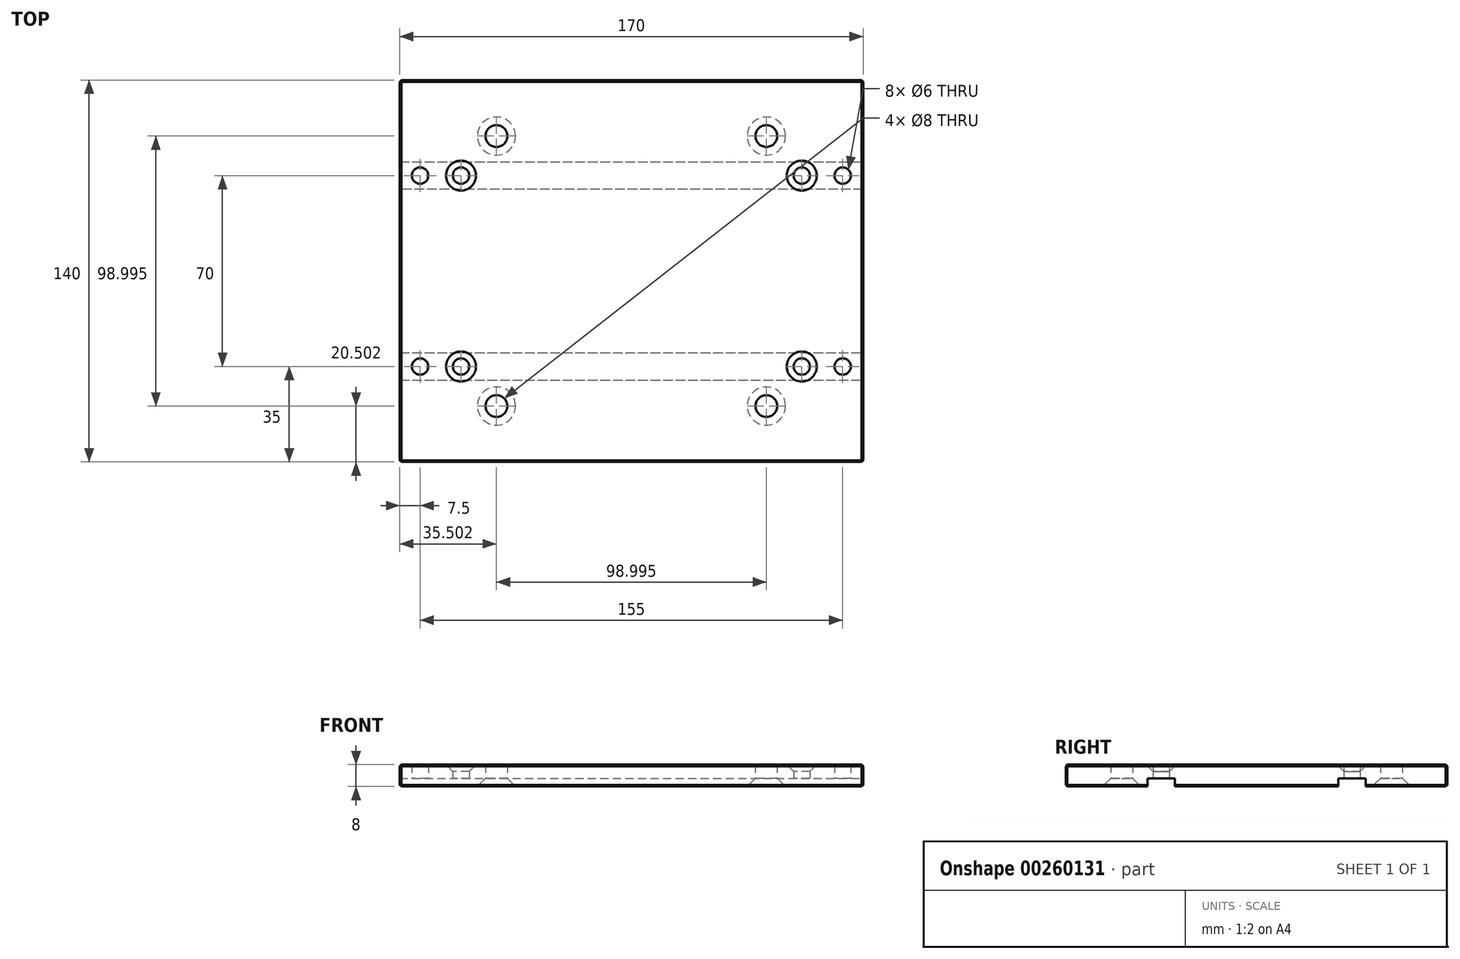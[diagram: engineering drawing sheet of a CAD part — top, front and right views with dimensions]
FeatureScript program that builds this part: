
annotation { "Feature Type Name" : "Feature", "Feature Type Description" : "" }
export const myFeature = defineFeature(function(context is Context, id is Id, definition is map)
    precondition{}
    {
        {
            var Q0;
            Q0=qCreatedBy(makeId("Top.planeOp"),FACE);
            var sketch = newSketch(context, id + "F0", { "sketchPlane" : qUnion([Q0])});
            skLineSegment(sketch, "E0.bottom", {"start": v(-85, -70) * mm, "end": v(85, -70) * mm});
            skLineSegment(sketch, "E0.top", {"start": v(-85, 70) * mm, "end": v(85, 70) * mm});
            skLineSegment(sketch, "E0.left", {"start": v(-85, -70) * mm, "end": v(-85, 70) * mm});
            skLineSegment(sketch, "E0.right", {"start": v(85, -70) * mm, "end": v(85, 70) * mm});
            skPoint(sketch, "E0.middle", {"position": v(0, 0) * mm});
            skCircle(sketch, "E1", {"center": v(0, 0) * mm, "radius": 70 * mm, "construction": true});
            skLineSegment(sketch, "E2", {"start": v(0, 0) * mm, "end": v(-49.5, 49.5) * mm, "construction": true});
            skLineSegment(sketch, "E3", {"start": v(-49.5, 49.5) * mm, "end": v(49.5, 49.5) * mm, "construction": true});
            skCircle(sketch, "E4", {"center": v(-49.5, 49.5) * mm, "radius": 4 * mm});
            skCircle(sketch, "E5", {"center": v(49.5, 49.5) * mm, "radius": 4 * mm});
            skCircle(sketch, "E6.MirrorC", {"center": v(49.5, -49.5) * mm, "radius": 4 * mm});
            skCircle(sketch, "E7.MirrorC", {"center": v(-49.5, -49.5) * mm, "radius": 4 * mm});
            skSolve(sketch);
        }
        {
            var Q0;
            Q0=makeQuery(id+"F0.imprint","IMPRINT",FACE,{"disambiguationData":[TD([[makeQuery(id+"F0.imprint","IMPRINT",EDGE,{"derivedFrom":sQuery(id+"F0.wireOp",EDGE,"E0.bottom")}),1.0]])]});
            extrude(context, id + "F1", {"entities" : qUnion([Q0]), "depth" : 8 * mm});
        }
        {
            var Q0;
            Q0=makeQuery(id+"F1.opExtrude","CAP_EDGE",EDGE,{"disambiguationData":[OSD([sQuery(id+"F0.wireOp",EDGE,"E7.MirrorC")])],"isStart":true});
            var Q1;
            Q1=makeQuery(id+"F1.opExtrude","CAP_EDGE",EDGE,{"disambiguationData":[OSD([sQuery(id+"F0.wireOp",EDGE,"E4")])],"isStart":true});
            var Q2;
            Q2=makeQuery(id+"F1.opExtrude","CAP_EDGE",EDGE,{"disambiguationData":[OSD([sQuery(id+"F0.wireOp",EDGE,"E5")])],"isStart":true});
            var Q3;
            Q3=makeQuery(id+"F1.opExtrude","CAP_EDGE",EDGE,{"disambiguationData":[OSD([sQuery(id+"F0.wireOp",EDGE,"E6.MirrorC")])],"isStart":true});
            chamfer(context, id + "F2", {"entities" : qUnion([Q0, Q1, Q2, Q3]), "width" : 3 * mm, "tangentPropagation" : true});
        }
        {
            var Q0;
            Q0=qCreatedBy(makeId("Top.planeOp"),FACE);
            var sketch = newSketch(context, id + "F3", { "sketchPlane" : qUnion([Q0])});
            skLineSegment(sketch, "E8", {"start": v(0, 0) * mm, "end": v(-90, 0) * mm, "construction": true});
            skLineSegment(sketch, "E9", {"start": v(-90, 0) * mm, "end": v(-90, -30) * mm, "construction": true});
            skLineSegment(sketch, "E10", {"start": v(-90, -30) * mm, "end": v(90, -30) * mm});
            skLineSegment(sketch, "E11", {"start": v(90, -30) * mm, "end": v(90, 30) * mm, "construction": true});
            skLineSegment(sketch, "E12", {"start": v(90, 30) * mm, "end": v(-90, 30) * mm});
            skLineSegment(sketch, "E13", {"start": v(-90, -30) * mm, "end": v(-90, -40) * mm});
            skLineSegment(sketch, "E14", {"start": v(-90, -40) * mm, "end": v(90, -40) * mm});
            skLineSegment(sketch, "E15", {"start": v(90, -40) * mm, "end": v(90, -30) * mm});
            skLineSegment(sketch, "E16", {"start": v(-90, 30) * mm, "end": v(-90, 40) * mm});
            skLineSegment(sketch, "E17", {"start": v(-90, 40) * mm, "end": v(90, 40) * mm});
            skLineSegment(sketch, "E18", {"start": v(90, 40) * mm, "end": v(90, 30) * mm});
            skSolve(sketch);
        }
        {
            var Q0;
            Q0=makeQuery(id+"F3.imprint","IMPRINT",FACE,{"disambiguationData":[TD([[makeQuery(id+"F3.imprint","IMPRINT",EDGE,{"derivedFrom":sQuery(id+"F3.wireOp",EDGE,"E10")}),-1.0]])]});
            var Q1;
            Q1=makeQuery(id+"F3.imprint","IMPRINT",FACE,{"disambiguationData":[TD([[makeQuery(id+"F3.imprint","IMPRINT",EDGE,{"derivedFrom":sQuery(id+"F3.wireOp",EDGE,"E12")}),-1.0]])]});
            extrude(context, id + "F4", {"entities" : qUnion([Q0, Q1]), "operationType" : NewBodyOperationType.REMOVE, "oppositeDirection" : true, "depth" : 25 * mm, "hasSecondDirection" : true, "secondDirectionOppositeDirection" : false, "secondDirectionDepth" : 3 * mm});
        }
        {
            var Q0;
            Q0=qCreatedBy(makeId("Top.planeOp"),FACE);
            var sketch = newSketch(context, id + "F5", { "sketchPlane" : qUnion([Q0])});
            skLineSegment(sketch, "E19", {"start": v(0, 0) * mm, "end": v(-85, 0) * mm, "construction": true});
            skLineSegment(sketch, "E20", {"start": v(-85, 0) * mm, "end": v(-85, -35) * mm, "construction": true});
            skLineSegment(sketch, "E21", {"start": v(-85, -35) * mm, "end": v(-62.5, -35) * mm, "construction": true});
            skLineSegment(sketch, "E22", {"start": v(-62.5, -35) * mm, "end": v(-62.5, -45) * mm, "construction": true});
            skLineSegment(sketch, "E23", {"start": v(-62.5, -45) * mm, "end": v(-77.5, -45) * mm, "construction": true});
            skLineSegment(sketch, "E24", {"start": v(-77.5, -45) * mm, "end": v(-77.5, -35) * mm, "construction": true});
            skCircle(sketch, "E25", {"center": v(-62.5, -35) * mm, "radius": 3 * mm});
            skCircle(sketch, "E26", {"center": v(-77.5, -35) * mm, "radius": 3 * mm});
            skCircle(sketch, "E27.MirrorC", {"center": v(-62.5, 35) * mm, "radius": 3 * mm});
            skCircle(sketch, "E28.MirrorC", {"center": v(-77.5, 35) * mm, "radius": 3 * mm});
            skCircle(sketch, "E29.MirrorC", {"center": v(62.5, 35) * mm, "radius": 3 * mm});
            skCircle(sketch, "E30.MirrorC", {"center": v(77.5, 35) * mm, "radius": 3 * mm});
            skCircle(sketch, "E31.MirrorC", {"center": v(62.5, -35) * mm, "radius": 3 * mm});
            skCircle(sketch, "E32.MirrorC", {"center": v(77.5, -35) * mm, "radius": 3 * mm});
            skSolve(sketch);
        }
        {
            var Q0;
            Q0 = qSketchRegion(id + "F5", true);
            extrude(context, id + "F6", {"entities" : qUnion([Q0]), "operationType" : NewBodyOperationType.REMOVE, "depth" : 25 * mm});
        }
        {
            var Q0;
            Q0=makeQuery(id+"F6.boolean.opBoolean","INTERSECT",EDGE,{"derivedFrom":[makeQuery(id+"F1.opExtrude","CAP_FACE",FACE,{"disambiguationData":[OSD([sQuery(id+"F0.wireOp",EDGE,"E0.bottom"),sQuery(id+"F0.wireOp",EDGE,"E0.top"),sQuery(id+"F0.wireOp",EDGE,"E0.left"),sQuery(id+"F0.wireOp",EDGE,"E0.right"),sQuery(id+"F0.wireOp",EDGE,"E4"),sQuery(id+"F0.wireOp",EDGE,"E5"),sQuery(id+"F0.wireOp",EDGE,"E6.MirrorC"),sQuery(id+"F0.wireOp",EDGE,"E7.MirrorC")])],"isStart":false}),makeQuery(id+"F6.opExtrude","SWEPT_FACE",FACE,{"disambiguationData":[OSD([sQuery(id+"F5.wireOp",EDGE,"E27.MirrorC")])]})]});
            var Q1;
            Q1=makeQuery(id+"F6.boolean.opBoolean","INTERSECT",EDGE,{"derivedFrom":[makeQuery(id+"F1.opExtrude","CAP_FACE",FACE,{"disambiguationData":[OSD([sQuery(id+"F0.wireOp",EDGE,"E0.bottom"),sQuery(id+"F0.wireOp",EDGE,"E0.top"),sQuery(id+"F0.wireOp",EDGE,"E0.left"),sQuery(id+"F0.wireOp",EDGE,"E0.right"),sQuery(id+"F0.wireOp",EDGE,"E4"),sQuery(id+"F0.wireOp",EDGE,"E5"),sQuery(id+"F0.wireOp",EDGE,"E6.MirrorC"),sQuery(id+"F0.wireOp",EDGE,"E7.MirrorC")])],"isStart":false}),makeQuery(id+"F6.opExtrude","SWEPT_FACE",FACE,{"disambiguationData":[OSD([sQuery(id+"F5.wireOp",EDGE,"E25")])]})]});
            var Q2;
            Q2=makeQuery(id+"F6.boolean.opBoolean","INTERSECT",EDGE,{"derivedFrom":[makeQuery(id+"F1.opExtrude","CAP_FACE",FACE,{"disambiguationData":[OSD([sQuery(id+"F0.wireOp",EDGE,"E0.bottom"),sQuery(id+"F0.wireOp",EDGE,"E0.top"),sQuery(id+"F0.wireOp",EDGE,"E0.left"),sQuery(id+"F0.wireOp",EDGE,"E0.right"),sQuery(id+"F0.wireOp",EDGE,"E4"),sQuery(id+"F0.wireOp",EDGE,"E5"),sQuery(id+"F0.wireOp",EDGE,"E6.MirrorC"),sQuery(id+"F0.wireOp",EDGE,"E7.MirrorC")])],"isStart":false}),makeQuery(id+"F6.opExtrude","SWEPT_FACE",FACE,{"disambiguationData":[OSD([sQuery(id+"F5.wireOp",EDGE,"E31.MirrorC")])]})]});
            var Q3;
            Q3=makeQuery(id+"F6.boolean.opBoolean","INTERSECT",EDGE,{"derivedFrom":[makeQuery(id+"F1.opExtrude","CAP_FACE",FACE,{"disambiguationData":[OSD([sQuery(id+"F0.wireOp",EDGE,"E0.bottom"),sQuery(id+"F0.wireOp",EDGE,"E0.top"),sQuery(id+"F0.wireOp",EDGE,"E0.left"),sQuery(id+"F0.wireOp",EDGE,"E0.right"),sQuery(id+"F0.wireOp",EDGE,"E4"),sQuery(id+"F0.wireOp",EDGE,"E5"),sQuery(id+"F0.wireOp",EDGE,"E6.MirrorC"),sQuery(id+"F0.wireOp",EDGE,"E7.MirrorC")])],"isStart":false}),makeQuery(id+"F6.opExtrude","SWEPT_FACE",FACE,{"disambiguationData":[OSD([sQuery(id+"F5.wireOp",EDGE,"E29.MirrorC")])]})]});
            chamfer(context, id + "F7", {"entities" : qUnion([Q0, Q1, Q2, Q3]), "width" : 2.5 * mm, "tangentPropagation" : true});
        }
        {
            var Q0;
            Q0=makeQuery(id+"F1.opExtrude","CAP_EDGE",EDGE,{"disambiguationData":[OSD([sQuery(id+"F0.wireOp",EDGE,"E0.left")])],"isStart":false});
            var Q1;
            Q1=makeQuery(id+"F1.opExtrude","CAP_EDGE",EDGE,{"disambiguationData":[OSD([sQuery(id+"F0.wireOp",EDGE,"E0.top")])],"isStart":false});
            var Q2;
            Q2=makeQuery(id+"F1.opExtrude","CAP_EDGE",EDGE,{"disambiguationData":[OSD([sQuery(id+"F0.wireOp",EDGE,"E0.bottom")])],"isStart":false});
            var Q3;
            Q3=makeQuery(id+"F1.opExtrude","CAP_EDGE",EDGE,{"disambiguationData":[OSD([sQuery(id+"F0.wireOp",EDGE,"E0.right")])],"isStart":false});
            var Q4;
            Q4=makeQuery(id+"F1.opExtrude","SWEPT_EDGE",EDGE,{"disambiguationData":[OSD([sQuery(id+"F0.wireOp",EDGE,"E0.bottom"),sQuery(id+"F0.wireOp",EDGE,"E0.right")])]});
            var Q5;
            Q5=makeQuery(id+"F1.opExtrude","SWEPT_EDGE",EDGE,{"disambiguationData":[OSD([sQuery(id+"F0.wireOp",EDGE,"E0.bottom"),sQuery(id+"F0.wireOp",EDGE,"E0.left")])]});
            var Q6;
            {var subQ0=sQuery(id+"F0.wireOp",EDGE,"E0.right");var subQ1=sQuery(id+"F0.wireOp",EDGE,"E0.top");Q6=makeQuery(id+"F4.boolean.opBoolean","SPLIT",EDGE,{"disambiguationData":[TD([makeQuery(id+"F1.opExtrude","SWEPT_FACE",FACE,{"disambiguationData":[OSD([subQ1])]})])],"derivedFrom":makeQuery(id+"F1.opExtrude","CAP_EDGE",EDGE,{"disambiguationData":[OSD([subQ0])],"isStart":true})});}
            var Q7;
            {var subQ0=sQuery(id+"F0.wireOp",EDGE,"E0.left");var subQ1=sQuery(id+"F0.wireOp",EDGE,"E0.top");Q7=makeQuery(id+"F4.boolean.opBoolean","SPLIT",EDGE,{"disambiguationData":[TD([makeQuery(id+"F1.opExtrude","SWEPT_FACE",FACE,{"disambiguationData":[OSD([subQ1])]})])],"derivedFrom":makeQuery(id+"F1.opExtrude","CAP_EDGE",EDGE,{"disambiguationData":[OSD([subQ0])],"isStart":true})});}
            var Q8;
            Q8=makeQuery(id+"F1.opExtrude","CAP_EDGE",EDGE,{"disambiguationData":[OSD([sQuery(id+"F0.wireOp",EDGE,"E0.top")])],"isStart":true});
            var Q9;
            {var subQ0=sQuery(id+"F0.wireOp",EDGE,"E0.left");Q9=makeQuery(id+"F4.boolean.opBoolean","SPLIT",EDGE,{"disambiguationData":[TD([makeQuery(id+"F4.opExtrude","SWEPT_FACE",FACE,{"disambiguationData":[OSD([sQuery(id+"F3.wireOp",EDGE,"E10")])]})])],"derivedFrom":makeQuery(id+"F1.opExtrude","CAP_EDGE",EDGE,{"disambiguationData":[OSD([subQ0])],"isStart":true})});}
            var Q10;
            {var subQ0=sQuery(id+"F0.wireOp",EDGE,"E0.bottom");var subQ1=sQuery(id+"F0.wireOp",EDGE,"E0.left");Q10=makeQuery(id+"F4.boolean.opBoolean","SPLIT",EDGE,{"disambiguationData":[TD([makeQuery(id+"F1.opExtrude","SWEPT_FACE",FACE,{"disambiguationData":[OSD([subQ0])]})])],"derivedFrom":makeQuery(id+"F1.opExtrude","CAP_EDGE",EDGE,{"disambiguationData":[OSD([subQ1])],"isStart":true})});}
            var Q11;
            {var subQ0=sQuery(id+"F0.wireOp",EDGE,"E0.right");Q11=makeQuery(id+"F4.boolean.opBoolean","SPLIT",EDGE,{"disambiguationData":[TD([makeQuery(id+"F4.opExtrude","SWEPT_FACE",FACE,{"disambiguationData":[OSD([sQuery(id+"F3.wireOp",EDGE,"E10")])]})])],"derivedFrom":makeQuery(id+"F1.opExtrude","CAP_EDGE",EDGE,{"disambiguationData":[OSD([subQ0])],"isStart":true})});}
            var Q12;
            {var subQ0=sQuery(id+"F0.wireOp",EDGE,"E0.bottom");var subQ1=sQuery(id+"F0.wireOp",EDGE,"E0.right");Q12=makeQuery(id+"F4.boolean.opBoolean","SPLIT",EDGE,{"disambiguationData":[TD([makeQuery(id+"F1.opExtrude","SWEPT_FACE",FACE,{"disambiguationData":[OSD([subQ0])]})])],"derivedFrom":makeQuery(id+"F1.opExtrude","CAP_EDGE",EDGE,{"disambiguationData":[OSD([subQ1])],"isStart":true})});}
            var Q13;
            Q13=makeQuery(id+"F1.opExtrude","CAP_EDGE",EDGE,{"disambiguationData":[OSD([sQuery(id+"F0.wireOp",EDGE,"E0.bottom")])],"isStart":true});
            var Q14;
            Q14=makeQuery(id+"F1.opExtrude","SWEPT_EDGE",EDGE,{"disambiguationData":[OSD([sQuery(id+"F0.wireOp",EDGE,"E0.top"),sQuery(id+"F0.wireOp",EDGE,"E0.right")])]});
            var Q15;
            Q15=makeQuery(id+"F1.opExtrude","SWEPT_EDGE",EDGE,{"disambiguationData":[OSD([sQuery(id+"F0.wireOp",EDGE,"E0.top"),sQuery(id+"F0.wireOp",EDGE,"E0.left")])]});
            chamfer(context, id + "F8", {"entities" : qUnion([Q0, Q1, Q2, Q3, Q4, Q5, Q6, Q7, Q8, Q9, Q10, Q11, Q12, Q13, Q14, Q15]), "width" : .6 * mm, "tangentPropagation" : true});
        }
    });
